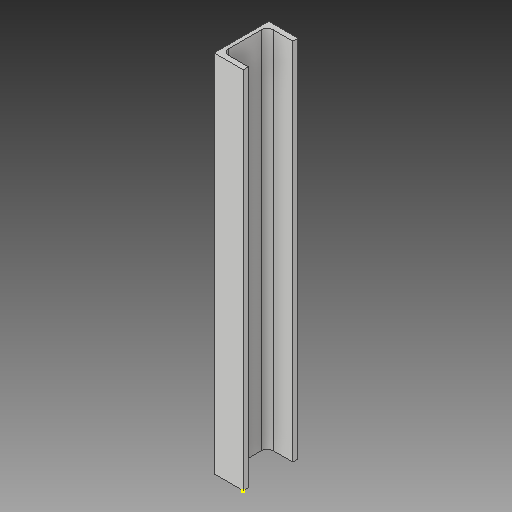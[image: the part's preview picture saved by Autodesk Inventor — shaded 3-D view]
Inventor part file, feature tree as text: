
AUTODESK INVENTOR PART (.ipt)
format: ipt  version: 2019 (Build 230136000, 136)  size: 98,304 bytes
history: native  units: mm
features: sketch x2, extrude x1
ambient origin geometry x8: Origin, YZ Plane, XZ Plane, XY Plane, X Axis, Y Axis, Z Axis, Center Point
bodies: Solid1 (feature_tree)
feature tree (3):
  sketch  "Sketch1"  dims[d0=40.0mm d1=75.0mm]
  extrude  "Extrusion1"  Depth=75.0mm
  sketch  "Sketch2"  dims[d2=40.0mm d3=7.0mm d5=35.0mm d6=61.0mm d7=8.0mm d8=500.0mm d9=0.0mm]
